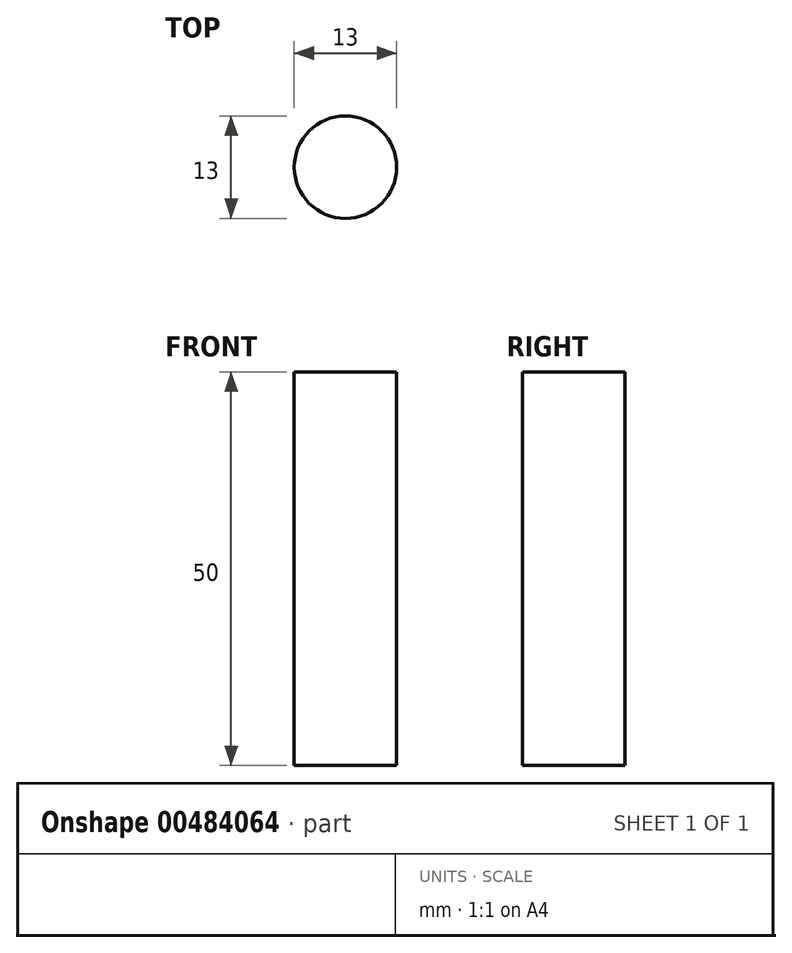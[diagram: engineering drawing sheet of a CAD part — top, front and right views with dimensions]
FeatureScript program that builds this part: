
annotation { "Feature Type Name" : "Feature", "Feature Type Description" : "" }
export const myFeature = defineFeature(function(context is Context, id is Id, definition is map)
    precondition{}
    {
        {
            var Q0;
            Q0=qCreatedBy(makeId("Top.planeOp"),FACE);
            var sketch = newSketch(context, id + "F0", { "sketchPlane" : qUnion([Q0])});
            skCircle(sketch, "E0", {"center": v(0, 0) * mm, "radius": 6.5 * mm});
            skSolve(sketch);
        }
        {
            var Q0;
            Q0 = qSketchRegion(id + "F0", true);
            extrude(context, id + "F1", {"entities" : qUnion([Q0]), "depth" : 50 * mm, "offsetDistance" : 25 * mm});
        }
    });
